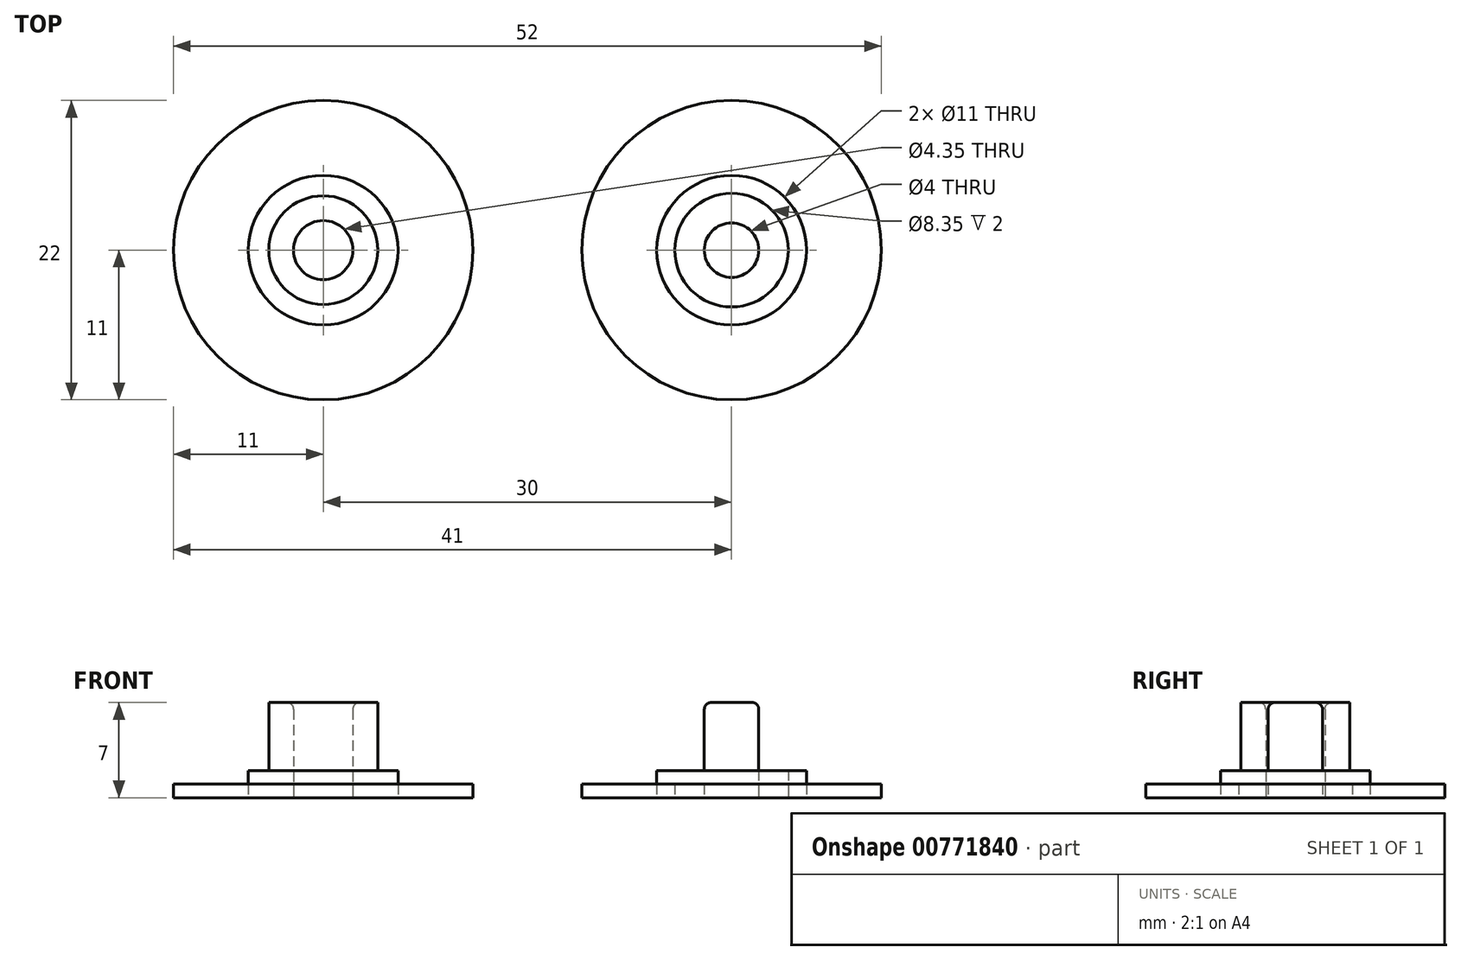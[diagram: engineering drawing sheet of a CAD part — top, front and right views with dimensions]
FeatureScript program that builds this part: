
annotation { "Feature Type Name" : "Feature", "Feature Type Description" : "" }
export const myFeature = defineFeature(function(context is Context, id is Id, definition is map)
    precondition{}
    {
        {
            var Q0;
            Q0=qCreatedBy(makeId("Top.planeOp"),FACE);
            var sketch = newSketch(context, id + "F0", { "sketchPlane" : qUnion([Q0])});
            skCircle(sketch, "E0", {"center": v(0, 0) * mm, "radius": 11 * mm});
            skCircle(sketch, "E1", {"center": v(0, 0) * mm, "radius": 5.5 * mm});
            skCircle(sketch, "E2", {"center": v(0, 0) * mm, "radius": 4 * mm});
            skCircle(sketch, "E3", {"center": v(0, 0) * mm, "radius": 2.17 * mm});
            skCircle(sketch, "E4", {"center": v(30, 0) * mm, "radius": 11 * mm});
            skCircle(sketch, "E5", {"center": v(30, 0) * mm, "radius": 5.5 * mm});
            skCircle(sketch, "E6", {"center": v(30, 0) * mm, "radius": 4.17 * mm});
            skCircle(sketch, "E7", {"center": v(30, 0) * mm, "radius": 2 * mm});
            skSolve(sketch);
        }
        {
            var Q0;
            Q0=makeQuery(id+"F0.imprint","IMPRINT",FACE,{"disambiguationData":[TD([[makeQuery(id+"F0.imprint","IMPRINT",EDGE,{"derivedFrom":sQuery(id+"F0.wireOp",EDGE,"E0")}),1.0]])]});
            var Q1;
            Q1=makeQuery(id+"F0.imprint","IMPRINT",FACE,{"disambiguationData":[TD([[makeQuery(id+"F0.imprint","IMPRINT",EDGE,{"derivedFrom":sQuery(id+"F0.wireOp",EDGE,"E4")}),1.0]])]});
            extrude(context, id + "F1", {"entities" : qUnion([Q0, Q1]), "depth" : 1 * mm, "offsetDistance" : 25 * mm});
        }
        {
            var Q0;
            Q0=makeQuery(id+"F0.imprint","IMPRINT",FACE,{"disambiguationData":[TD([[makeQuery(id+"F0.imprint","IMPRINT",EDGE,{"derivedFrom":sQuery(id+"F0.wireOp",EDGE,"E1")}),1.0]])]});
            var Q1;
            Q1=makeQuery(id+"F0.imprint","IMPRINT",FACE,{"disambiguationData":[TD([[makeQuery(id+"F0.imprint","IMPRINT",EDGE,{"derivedFrom":sQuery(id+"F0.wireOp",EDGE,"E5")}),1.0]])]});
            extrude(context, id + "F2", {"entities" : qUnion([Q0, Q1]), "depth" : 2 * mm, "offsetDistance" : 25 * mm});
        }
        {
            var Q0;
            Q0=makeQuery(id+"F0.imprint","IMPRINT",FACE,{"disambiguationData":[TD([[makeQuery(id+"F0.imprint","IMPRINT",EDGE,{"derivedFrom":sQuery(id+"F0.wireOp",EDGE,"E2")}),1.0]])]});
            var Q1;
            Q1=makeQuery(id+"F0.imprint","IMPRINT",FACE,{"disambiguationData":[TD([[makeQuery(id+"F0.imprint","IMPRINT",EDGE,{"derivedFrom":sQuery(id+"F0.wireOp",EDGE,"E7")}),1.0]])]});
            extrude(context, id + "F3", {"entities" : qUnion([Q0, Q1]), "operationType" : NewBodyOperationType.ADD, "depth" : 7 * mm, "offsetDistance" : 25 * mm});
        }
        {
            var Q0;
            Q0=makeQuery(id+"F0.imprint","IMPRINT",FACE,{"disambiguationData":[TD([[makeQuery(id+"F0.imprint","IMPRINT",EDGE,{"derivedFrom":sQuery(id+"F0.wireOp",EDGE,"E6")}),1.0]])]});
            var Q1;
            Q1=makeQuery(id+"F0.imprint","IMPRINT",FACE,{"disambiguationData":[TD([[makeQuery(id+"F0.imprint","IMPRINT",EDGE,{"derivedFrom":sQuery(id+"F0.wireOp",EDGE,"E3")}),1.0]])]});
            extrude(context, id + "F4", {"entities" : qUnion([Q0, Q1]), "depth" : 1 * mm, "offsetDistance" : 25 * mm});
        }
        {
            var Q0;
            Q0=makeQuery(id+"F3.opExtrude","CAP_EDGE",EDGE,{"disambiguationData":[OSD([sQuery(id+"F0.wireOp",EDGE,"E7")])],"isStart":false});
            var Q1;
            Q1=makeQuery(id+"F3.opExtrude","CAP_EDGE",EDGE,{"disambiguationData":[OSD([sQuery(id+"F0.wireOp",EDGE,"E3")])],"isStart":false});
            fillet(context, id + "F5", {"entities" : qUnion([Q0, Q1]), "radius" : 0.5 * mm, "tangentPropagation" : true, "allowEdgeOverflow" : false});
        }
    });
